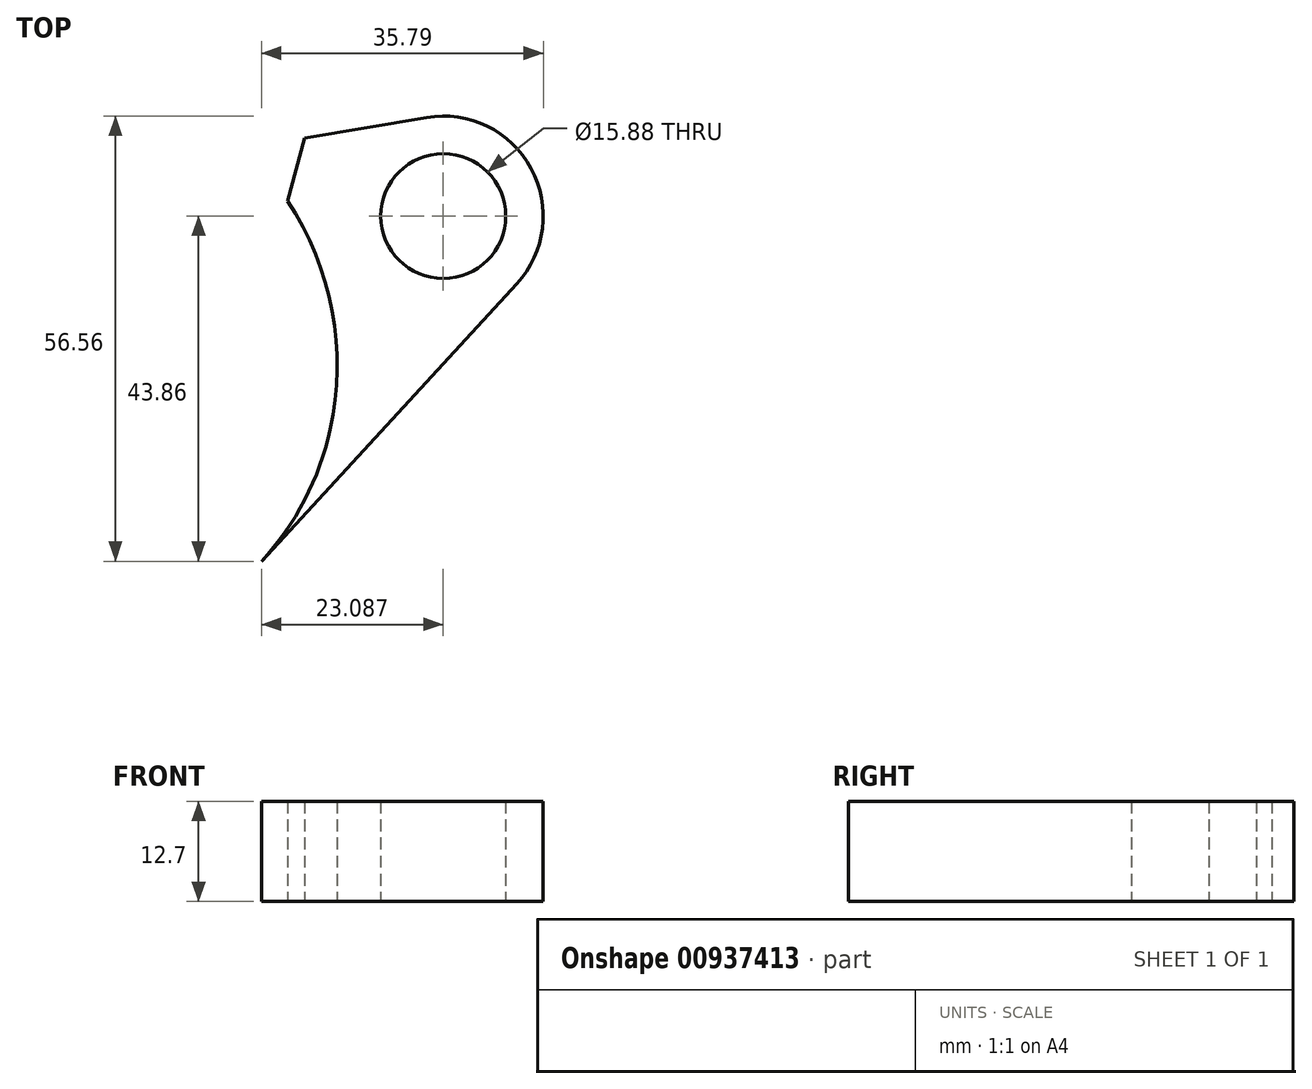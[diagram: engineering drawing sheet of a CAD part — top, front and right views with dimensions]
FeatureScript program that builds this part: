
annotation { "Feature Type Name" : "Feature", "Feature Type Description" : "" }
export const myFeature = defineFeature(function(context is Context, id is Id, definition is map)
    precondition{}
    {
        {
            var Q0;
            Q0=qCreatedBy(makeId("Top.planeOp"),FACE);
            var sketch = newSketch(context, id + "F0", { "sketchPlane" : qUnion([Q0])});
            skArc(sketch, "E0", {"start": v(-26.19, 0) * mm, "mid": v(0, -26.19) * mm, "end": v(26.19, 0) * mm});
            skArc(sketch, "E1", {"start": v(37.24, -8.07) * mm, "mid": v(36.4, 11.25) * mm, "end": v(26.19, 27.67) * mm});
            skLineSegment(sketch, "E2", {"start": v(26.19, 0) * mm, "end": v(26.19, 22.3) * mm});
            skArc(sketch, "E3", {"start": v(-28.76, 19.63) * mm, "mid": v(-12.34, -33.72) * mm, "end": v(37.24, -8.07) * mm});
            skCircle(sketch, "E4", {"center": v(51.59, 19.05) * mm, "radius": 7.94 * mm});
            skCircle(sketch, "E5", {"center": v(51.59, 19.05) * mm, "radius": 12.7 * mm});
            skLineSegment(sketch, "E6", {"start": v(60.93, 10.45) * mm, "end": v(28.5, -24.8) * mm});
            skLineSegment(sketch, "E7", {"start": v(49.5, 31.58) * mm, "end": v(31.49, 28.56) * mm});
            skPoint(sketch, "E8.orphan", {"position": v(38.1, 0) * mm});
            skArc(sketch, "E9", {"start": v(-26.19, 18.47) * mm, "mid": v(-27.12, 20.11) * mm, "end": v(-28.88, 19.44) * mm});
            skPoint(sketch, "E9.first.point", {"position": v(-28.2, 17.43) * mm});
            skPoint(sketch, "E9.second.point", {"position": v(-26.19, 18.47) * mm});
            skPoint(sketch, "E9.third.point", {"position": v(-28.76, 19.63) * mm});
            skPoint(sketch, "E10.visualSharp", {"position": v(26.19, 27.67) * mm});
            skArc(sketch, "E10.filletArc", {"start": v(31.49, 28.56) * mm, "mid": v(27.7, 26.4) * mm, "end": v(26.19, 22.3) * mm});
            skLineSegment(sketch, "E11", {"start": v(26.19, 0) * mm, "end": v(38.47, 45.83) * mm});
            skLineSegment(sketch, "E12", {"start": v(-26.19, 0) * mm, "end": v(-14.34, 44.21) * mm});
            skSolve(sketch);
        }
        {
            var Q0;
            {var subQ6=sQuery(id+"F0.wireOp",EDGE,"E0");Q0=makeQuery(id+"F0.imprint","IMPRINT",FACE,{"disambiguationData":[TD([[makeQuery(id+"F0.imprint","IMPRINT",EDGE,{"derivedFrom":subQ6}),-1.0]])]});}
            var Q1;
            {var subQ0=sQuery(id+"F0.wireOp",EDGE,"E6");Q1=makeQuery(id+"F0.imprint","IMPRINT",FACE,{"disambiguationData":[TD([[makeQuery(id+"F0.imprint","IMPRINT",EDGE,{"derivedFrom":subQ0}),-1.0]])]});}
            var Q2;
            Q2=makeQuery(id+"F0.imprint","IMPRINT",FACE,{"disambiguationData":[TD([[makeQuery(id+"F0.imprint","IMPRINT",EDGE,{"derivedFrom":sQuery(id+"F0.wireOp",EDGE,"E4")}),-1.0]])]});
            extrude(context, id + "F1", {"entities" : qUnion([Q0, Q1, Q2]), "depth" : 12.7 * mm, "offsetDistance" : 25.4 * mm});
        }
    });
